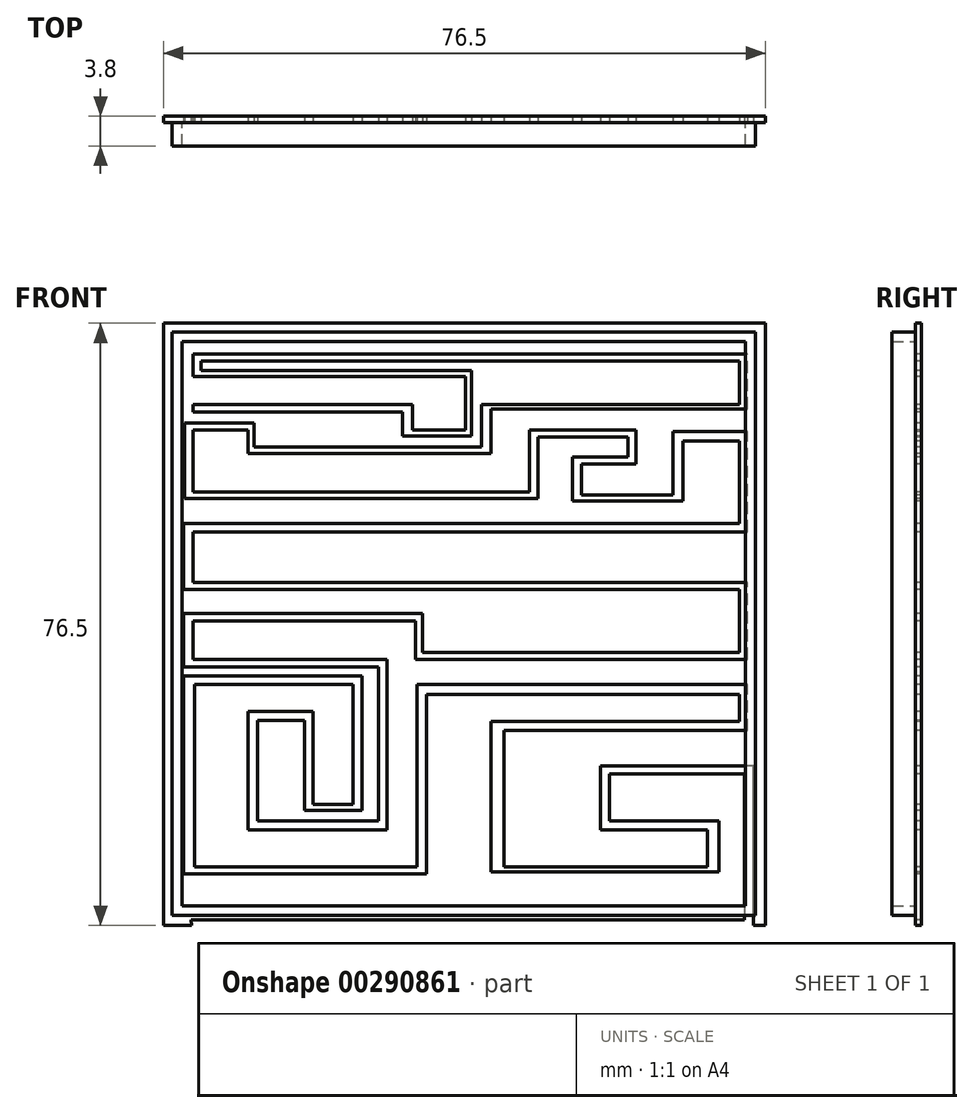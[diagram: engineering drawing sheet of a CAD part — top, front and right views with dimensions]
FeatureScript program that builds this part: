
annotation { "Feature Type Name" : "Feature", "Feature Type Description" : "" }
export const myFeature = defineFeature(function(context is Context, id is Id, definition is map)
    precondition{}
    {
        {
            var Q0;
            Q0=qCreatedBy(makeId("Front.planeOp"),FACE);
            var sketch = newSketch(context, id + "F0", { "sketchPlane" : qUnion([Q0])});
            skLineSegment(sketch, "E0.bottom", {"start": v(0, 0) * mm, "end": v(-76.5, 0) * mm});
            skLineSegment(sketch, "E0.top", {"start": v(0, 76.5) * mm, "end": v(-76.5, 76.5) * mm});
            skLineSegment(sketch, "E0.left", {"start": v(0, 0) * mm, "end": v(0, 76.5) * mm});
            skLineSegment(sketch, "E0.right", {"start": v(-76.5, 0) * mm, "end": v(-76.5, 76.5) * mm});
            skSolve(sketch);
        }
        {
            var Q0;
            Q0 = qSketchRegion(id + "F0", true);
            extrude(context, id + "F1", {"entities" : qUnion([Q0]), "depth" : .795 * mm});
        }
        {
            var Q0;
            Q0=makeQuery(id+"F1.opExtrude","CAP_FACE",FACE,{"disambiguationData":[OSD([sQuery(id+"F0.wireOp",EDGE,"E0.bottom"),sQuery(id+"F0.wireOp",EDGE,"E0.top"),sQuery(id+"F0.wireOp",EDGE,"E0.left"),sQuery(id+"F0.wireOp",EDGE,"E0.right")])],"isStart":false});
            var sketch = newSketch(context, id + "F2", { "sketchPlane" : qUnion([Q0])});
            skLineSegment(sketch, "E1.bottom", {"start": v(-75.39, 75.39) * mm, "end": v(-1.3, 75.4) * mm});
            skLineSegment(sketch, "E1.top", {"start": v(-75.39, 1.3) * mm, "end": v(-1.3, 1.3) * mm});
            skLineSegment(sketch, "E1.left", {"start": v(-75.39, 75.39) * mm, "end": v(-75.39, 1.3) * mm});
            skLineSegment(sketch, "E1.right", {"start": v(-1.3, 75.4) * mm, "end": v(-1.3, 1.3) * mm});
            skPoint(sketch, "E1.middle", {"position": v(-38.34, 38.35) * mm});
            skLineSegment(sketch, "E2.bottom", {"start": v(-74.12, 74.19) * mm, "end": v(-2.57, 74.19) * mm});
            skLineSegment(sketch, "E2.top", {"start": v(-74.12, 2.5) * mm, "end": v(-2.57, 2.5) * mm});
            skLineSegment(sketch, "E2.left", {"start": v(-74.12, 74.19) * mm, "end": v(-74.12, 2.5) * mm});
            skLineSegment(sketch, "E2.right", {"start": v(-2.57, 74.19) * mm, "end": v(-2.57, 2.5) * mm});
            skSolve(sketch);
        }
        {
            var Q0;
            Q0=makeQuery(id+"F2.imprint","IMPRINT",FACE,{"disambiguationData":[TD([[makeQuery(id+"F2.imprint","IMPRINT",EDGE,{"derivedFrom":sQuery(id+"F2.wireOp",EDGE,"E1.bottom")}),-1.0]])]});
            extrude(context, id + "F3", {"entities" : qUnion([Q0]), "operationType" : NewBodyOperationType.ADD, "depth" : 3 * mm});
        }
        {
            var Q0;
            Q0=makeQuery(id+"F3.boolean.opBoolean","SPLIT",FACE,{"disambiguationData":[TD([makeQuery(id+"F3.opExtrude","SWEPT_FACE",FACE,{"disambiguationData":[OSD([sQuery(id+"F2.wireOp",EDGE,"E2.bottom")])]})])],"derivedFrom":makeQuery(id+"F1.opExtrude","CAP_FACE",FACE,{"disambiguationData":[OSD([sQuery(id+"F0.wireOp",EDGE,"E0.bottom"),sQuery(id+"F0.wireOp",EDGE,"E0.top"),sQuery(id+"F0.wireOp",EDGE,"E0.left"),sQuery(id+"F0.wireOp",EDGE,"E0.right")])],"isStart":false})});
            var sketch = newSketch(context, id + "F4", { "sketchPlane" : qUnion([Q0])});
            skLineSegment(sketch, "E3", {"start": v(-72.87, -0.5) * mm, "end": v(-1.54, -0.5) * mm});
            skLineSegment(sketch, "E4", {"start": v(-1.54, -0.5) * mm, "end": v(-1.54, 20.23) * mm});
            skLineSegment(sketch, "E5", {"start": v(-1.54, 20.23) * mm, "end": v(-20.98, 20.23) * mm});
            skLineSegment(sketch, "E6", {"start": v(-20.98, 20.23) * mm, "end": v(-20.98, 12.14) * mm});
            skLineSegment(sketch, "E7", {"start": v(-20.98, 12.14) * mm, "end": v(-7.43, 12.14) * mm});
            skLineSegment(sketch, "E8", {"start": v(-7.43, 12.14) * mm, "end": v(-7.43, 7.43) * mm});
            skLineSegment(sketch, "E9", {"start": v(-7.43, 7.43) * mm, "end": v(-33.21, 7.43) * mm});
            skLineSegment(sketch, "E10", {"start": v(-33.21, 7.43) * mm, "end": v(-33.21, 24.75) * mm});
            skLineSegment(sketch, "E11", {"start": v(-33.21, 24.75) * mm, "end": v(-2.34, 24.75) * mm});
            skLineSegment(sketch, "E12", {"start": v(-2.34, 24.75) * mm, "end": v(-2.34, 30.58) * mm});
            skLineSegment(sketch, "E13", {"start": v(-2.34, 30.58) * mm, "end": v(-44.32, 30.58) * mm});
            skLineSegment(sketch, "E14", {"start": v(-44.32, 30.58) * mm, "end": v(-44.32, 7.43) * mm});
            skLineSegment(sketch, "E15", {"start": v(-44.32, 7.43) * mm, "end": v(-72.55, 7.43) * mm});
            skLineSegment(sketch, "E16", {"start": v(-72.55, 7.43) * mm, "end": v(-72.55, 30.58) * mm});
            skLineSegment(sketch, "E17", {"start": v(-72.55, 30.58) * mm, "end": v(-52.4, 30.58) * mm});
            skLineSegment(sketch, "E18", {"start": v(-52.4, 30.58) * mm, "end": v(-52.4, 15.34) * mm});
            skLineSegment(sketch, "E19", {"start": v(-52.4, 15.34) * mm, "end": v(-57.5, 15.34) * mm});
            skLineSegment(sketch, "E20", {"start": v(-57.5, 15.34) * mm, "end": v(-57.5, 27.2) * mm});
            skLineSegment(sketch, "E21", {"start": v(-57.5, 27.2) * mm, "end": v(-65.77, 27.2) * mm});
            skLineSegment(sketch, "E22", {"start": v(-65.77, 27.2) * mm, "end": v(-65.77, 12.14) * mm});
            skLineSegment(sketch, "E23", {"start": v(-65.77, 12.14) * mm, "end": v(-48.08, 12.14) * mm});
            skLineSegment(sketch, "E24", {"start": v(-48.08, 12.14) * mm, "end": v(-48.08, 33.78) * mm});
            skLineSegment(sketch, "E25", {"start": v(-48.08, 33.78) * mm, "end": v(-72.74, 33.78) * mm});
            skLineSegment(sketch, "E26", {"start": v(-72.74, 33.78) * mm, "end": v(-72.74, 38.68) * mm});
            skLineSegment(sketch, "E27", {"start": v(-72.74, 38.68) * mm, "end": v(-44.5, 38.68) * mm});
            skLineSegment(sketch, "E28", {"start": v(-44.5, 38.68) * mm, "end": v(-44.5, 33.78) * mm});
            skLineSegment(sketch, "E29", {"start": v(-44.5, 33.78) * mm, "end": v(-2.34, 33.78) * mm});
            skLineSegment(sketch, "E30", {"start": v(-2.34, 33.78) * mm, "end": v(-2.34, 43.57) * mm});
            skLineSegment(sketch, "E31", {"start": v(-2.34, 43.57) * mm, "end": v(-72.74, 43.57) * mm});
            skLineSegment(sketch, "E32", {"start": v(-72.74, 43.57) * mm, "end": v(-72.74, 49.97) * mm});
            skLineSegment(sketch, "E33", {"start": v(-72.74, 49.97) * mm, "end": v(-2.34, 49.97) * mm});
            skLineSegment(sketch, "E34", {"start": v(-2.34, 49.97) * mm, "end": v(-2.34, 62.77) * mm});
            skLineSegment(sketch, "E35", {"start": v(-2.34, 62.77) * mm, "end": v(-11.76, 62.77) * mm});
            skLineSegment(sketch, "E36", {"start": v(-11.76, 62.77) * mm, "end": v(-11.76, 54.68) * mm});
            skLineSegment(sketch, "E37", {"start": v(-11.76, 54.68) * mm, "end": v(-23.42, 54.68) * mm});
            skLineSegment(sketch, "E38", {"start": v(-23.42, 54.68) * mm, "end": v(-23.42, 58.63) * mm});
            skLineSegment(sketch, "E39", {"start": v(-23.42, 58.63) * mm, "end": v(-16.46, 58.63) * mm});
            skLineSegment(sketch, "E40", {"start": v(-16.46, 58.63) * mm, "end": v(-16.46, 62.96) * mm});
            skLineSegment(sketch, "E41", {"start": v(-16.46, 62.96) * mm, "end": v(-30.01, 62.96) * mm});
            skLineSegment(sketch, "E42", {"start": v(-30.01, 62.96) * mm, "end": v(-30.01, 55.05) * mm});
            skLineSegment(sketch, "E43", {"start": v(-30.01, 55.05) * mm, "end": v(-72.74, 55.05) * mm});
            skLineSegment(sketch, "E44", {"start": v(-72.74, 55.05) * mm, "end": v(-72.74, 62.96) * mm});
            skLineSegment(sketch, "E45", {"start": v(-72.74, 62.96) * mm, "end": v(-65.77, 62.96) * mm});
            skLineSegment(sketch, "E46", {"start": v(-65.77, 62.96) * mm, "end": v(-65.77, 59.95) * mm});
            skLineSegment(sketch, "E47", {"start": v(-65.77, 59.95) * mm, "end": v(-34.9, 59.95) * mm});
            skLineSegment(sketch, "E48", {"start": v(-34.9, 59.95) * mm, "end": v(-34.9, 65.6) * mm});
            skLineSegment(sketch, "E49", {"start": v(-34.9, 65.6) * mm, "end": v(-2.34, 65.6) * mm});
            skLineSegment(sketch, "E50", {"start": v(-2.34, 65.6) * mm, "end": v(-2.34, 72.56) * mm});
            skLineSegment(sketch, "E51", {"start": v(-2.34, 72.56) * mm, "end": v(-72.74, 72.56) * mm});
            skLineSegment(sketch, "E52", {"start": v(-72.74, 72.56) * mm, "end": v(-72.74, 69.73) * mm});
            skLineSegment(sketch, "E53", {"start": v(-72.74, 69.73) * mm, "end": v(-38.1, 69.73) * mm});
            skLineSegment(sketch, "E54", {"start": v(-38.1, 69.73) * mm, "end": v(-38.1, 62.96) * mm});
            skLineSegment(sketch, "E55", {"start": v(-38.1, 62.96) * mm, "end": v(-44.88, 62.96) * mm});
            skLineSegment(sketch, "E56", {"start": v(-44.88, 62.96) * mm, "end": v(-44.88, 66.16) * mm});
            skLineSegment(sketch, "E57", {"start": v(-44.88, 66.16) * mm, "end": v(-72.74, 66.16) * mm});
            skLineSegment(sketch, "E58", {"start": v(-72.74, 66.16) * mm, "end": v(-72.74, 65.21) * mm});
            skLineSegment(sketch, "E59", {"start": v(-72.74, 65.21) * mm, "end": v(-46.14, 65.21) * mm});
            skLineSegment(sketch, "E60", {"start": v(-46.14, 65.21) * mm, "end": v(-46.14, 62.15) * mm});
            skLineSegment(sketch, "E61", {"start": v(-46.14, 62.15) * mm, "end": v(-37.37, 62.15) * mm});
            skLineSegment(sketch, "E62", {"start": v(-37.37, 62.15) * mm, "end": v(-37.37, 70.5) * mm});
            skLineSegment(sketch, "E63", {"start": v(-37.37, 70.5) * mm, "end": v(-71.73, 70.5) * mm});
            skLineSegment(sketch, "E64", {"start": v(-71.73, 70.5) * mm, "end": v(-71.73, 71.66) * mm});
            skLineSegment(sketch, "E65", {"start": v(-71.73, 71.66) * mm, "end": v(-3.32, 71.66) * mm});
            skLineSegment(sketch, "E66", {"start": v(-3.32, 71.66) * mm, "end": v(-3.32, 66.16) * mm});
            skLineSegment(sketch, "E67", {"start": v(-3.32, 66.16) * mm, "end": v(-36.1, 66.16) * mm});
            skLineSegment(sketch, "E68", {"start": v(-36.1, 66.16) * mm, "end": v(-36.1, 60.77) * mm});
            skLineSegment(sketch, "E69", {"start": v(-36.1, 60.77) * mm, "end": v(-64.96, 60.77) * mm});
            skLineSegment(sketch, "E70", {"start": v(-64.96, 60.77) * mm, "end": v(-64.96, 63.84) * mm});
            skLineSegment(sketch, "E71", {"start": v(-64.96, 63.84) * mm, "end": v(-73.84, 63.84) * mm});
            skLineSegment(sketch, "E72", {"start": v(-73.84, 63.84) * mm, "end": v(-73.84, 54.22) * mm});
            skLineSegment(sketch, "E73", {"start": v(-73.84, 54.22) * mm, "end": v(-28.9, 54.22) * mm});
            skLineSegment(sketch, "E74", {"start": v(-28.9, 54.22) * mm, "end": v(-28.9, 62.04) * mm});
            skLineSegment(sketch, "E75", {"start": v(-28.9, 62.04) * mm, "end": v(-17.49, 62.04) * mm});
            skLineSegment(sketch, "E76", {"start": v(-17.49, 62.04) * mm, "end": v(-17.49, 59.5) * mm});
            skLineSegment(sketch, "E77", {"start": v(-17.49, 59.5) * mm, "end": v(-24.57, 59.5) * mm});
            skLineSegment(sketch, "E78", {"start": v(-24.57, 59.5) * mm, "end": v(-24.57, 53.9) * mm});
            skLineSegment(sketch, "E79", {"start": v(-24.57, 53.9) * mm, "end": v(-10.51, 53.9) * mm});
            skLineSegment(sketch, "E80", {"start": v(-10.51, 53.9) * mm, "end": v(-10.51, 61.51) * mm});
            skLineSegment(sketch, "E81", {"start": v(-10.51, 61.51) * mm, "end": v(-3.32, 61.51) * mm});
            skLineSegment(sketch, "E82", {"start": v(-3.32, 61.51) * mm, "end": v(-3.32, 51.04) * mm});
            skLineSegment(sketch, "E83", {"start": v(-3.32, 51.04) * mm, "end": v(-73.95, 51.04) * mm});
            skLineSegment(sketch, "E84", {"start": v(-73.95, 51.04) * mm, "end": v(-73.95, 42.7) * mm});
            skLineSegment(sketch, "E85", {"start": v(-73.95, 42.7) * mm, "end": v(-3.32, 42.7) * mm});
            skLineSegment(sketch, "E86", {"start": v(-3.32, 42.7) * mm, "end": v(-3.32, 34.66) * mm});
            skLineSegment(sketch, "E87", {"start": v(-3.32, 34.66) * mm, "end": v(-43.6, 34.66) * mm});
            skLineSegment(sketch, "E88", {"start": v(-43.6, 34.66) * mm, "end": v(-43.6, 39.62) * mm});
            skLineSegment(sketch, "E89", {"start": v(-43.6, 39.62) * mm, "end": v(-73.95, 39.62) * mm});
            skLineSegment(sketch, "E90", {"start": v(-73.95, 39.62) * mm, "end": v(-73.95, 32.86) * mm});
            skLineSegment(sketch, "E91", {"start": v(-73.95, 32.86) * mm, "end": v(-49.2, 32.86) * mm});
            skLineSegment(sketch, "E92", {"start": v(-49.2, 32.86) * mm, "end": v(-49.2, 13.28) * mm});
            skLineSegment(sketch, "E93", {"start": v(-49.2, 13.28) * mm, "end": v(-64.57, 13.28) * mm});
            skLineSegment(sketch, "E94", {"start": v(-64.57, 13.28) * mm, "end": v(-64.57, 26.01) * mm});
            skLineSegment(sketch, "E95", {"start": v(-64.57, 26.01) * mm, "end": v(-58.6, 26.01) * mm});
            skLineSegment(sketch, "E96", {"start": v(-58.6, 26.01) * mm, "end": v(-58.6, 14.6) * mm});
            skLineSegment(sketch, "E97", {"start": v(-58.6, 14.6) * mm, "end": v(-51.3, 14.6) * mm});
            skLineSegment(sketch, "E98", {"start": v(-51.3, 14.6) * mm, "end": v(-51.3, 31.72) * mm});
            skLineSegment(sketch, "E99", {"start": v(-51.3, 31.72) * mm, "end": v(-73.95, 31.72) * mm});
            skLineSegment(sketch, "E100", {"start": v(-73.95, 31.72) * mm, "end": v(-73.95, 6.51) * mm});
            skLineSegment(sketch, "E101", {"start": v(-73.95, 6.51) * mm, "end": v(-43.08, 6.51) * mm});
            skLineSegment(sketch, "E102", {"start": v(-43.08, 6.51) * mm, "end": v(-43.08, 29.33) * mm});
            skLineSegment(sketch, "E103", {"start": v(-43.08, 29.33) * mm, "end": v(-3.32, 29.33) * mm});
            skLineSegment(sketch, "E104", {"start": v(-3.32, 29.33) * mm, "end": v(-3.32, 25.88) * mm});
            skLineSegment(sketch, "E105", {"start": v(-3.32, 25.88) * mm, "end": v(-34.9, 25.88) * mm});
            skLineSegment(sketch, "E106", {"start": v(-34.9, 25.88) * mm, "end": v(-34.9, 6.78) * mm});
            skLineSegment(sketch, "E107", {"start": v(-34.9, 6.78) * mm, "end": v(-5.94, 6.78) * mm});
            skLineSegment(sketch, "E108", {"start": v(-5.94, 6.78) * mm, "end": v(-5.94, 13.28) * mm});
            skLineSegment(sketch, "E109", {"start": v(-5.94, 13.28) * mm, "end": v(-19.87, 13.28) * mm});
            skLineSegment(sketch, "E110", {"start": v(-19.87, 13.28) * mm, "end": v(-19.87, 19.25) * mm});
            skLineSegment(sketch, "E111", {"start": v(-19.87, 19.25) * mm, "end": v(-2.67, 19.25) * mm});
            skLineSegment(sketch, "E112", {"start": v(-2.67, 19.25) * mm, "end": v(-2.67, 0.73) * mm});
            skLineSegment(sketch, "E113", {"start": v(-2.67, 0.73) * mm, "end": v(-72.97, 0.73) * mm});
            skLineSegment(sketch, "E114", {"start": v(-72.97, 0.73) * mm, "end": v(-72.87, -0.5) * mm});
            skSolve(sketch);
        }
        {
            var Q0;
            Q0 = qSketchRegion(id + "F4", true);
            extrude(context, id + "F5", {"entities" : qUnion([Q0]), "operationType" : NewBodyOperationType.REMOVE, "oppositeDirection" : true, "depth" : .795 * mm});
        }
    });
